FCSTD DOCUMENT  (FreeCAD 0.20R29410 (Git))
Label: wearableV5_April_07_2023
License: All rights reserved
LicenseURL: http://en.wikipedia.org/wiki/All_rights_reserved
objects: Part::Feature×60, Part::Cylinder×20, Part::MultiFuse×15, Sketcher::SketchObject×13, Part::Extrusion×13, Part::Fillet×12, App::Part×9, Part::Box×5, Part::Cut×5, Mesh::Feature×3, Part::Compound×1
note: 144 computed .brp shape members not serialized (recipe doc carries the construction recipe); baked Part::Feature solids carry a one-line shape summary decoded from their .brp

FEATURE [Part::Box] Box  label="battery"
  AttacherType = Attacher::AttachEngine3D
  Height = 11
  Length = 65
  Placement = pos=(4,2,2) rot=(0,0,1;0rad)
  Width = 30
FEATURE [Mesh::Feature] pisugar3Board
  Placement = pos=(-2.89,35.08,0.25) rot=(-1,0,0;4.71239rad)
FEATURE [Part::Feature] Part__Feature001  label="RaspberryPiZeroW"
  Placement = pos=(36.5,17,19.18) rot=(1,0,0;1.5708rad)
  shape: bbox 65.9 x 31.25 x 4.8 mm, 368 faces, 2 solids (baked)
FEATURE [Part::Feature] Part__Feature  label="ips7100"
  Placement = pos=(-24,0,222) rot=(0.999993,-0.003655,0;3.14159rad)
  shape: bbox 48.14 x 14.05 x 44.14 mm, 1935 faces (baked)
FEATURE [Part::Compound] Compound  label="ips7100s"
  Links = -> [Part__Feature]
  Placement = pos=(12.15,32.5,15.79) rot=(0,0.707107,0.707107;3.15032rad)
FEATURE [Part::Feature] Part__Feature002  label="Printed Circuit Board"
  shape: bbox 25.4 x 17.78 x 1.6 mm, 42 faces (baked)
FEATURE [Part::Feature] Part__Feature003  label="EAHC2835WD6"
  shape: bbox 3.513 x 2.813 x 0.7485 mm, 108 faces, 4 solids (baked)
FEATURE [Part::Feature] Part__Feature004  label="AS7341 v2"
  Placement = pos=(0,-0.339822,1.6) rot=(0,0,1;0rad)
  shape: bbox 2 x 3.1 x 1.1 mm, 267 faces, 26 solids (baked)
FEATURE [Part::Feature] Part__Feature005  label="CAPC-0805-T0.95-BN v1"
  Placement = pos=(-5.01759,-3.15294,1.6) rot=(0,0,1;0rad)
  shape: bbox 2.1 x 1.35 x 0.95 mm, 42 faces (baked)
FEATURE [Part::Feature] Part__Feature006  label="CAPC-0805-T0.95-BN v002"
  Placement = pos=(-5.48627,2.66154,1.6) rot=(0,0,-1;1.5708rad)
  shape: bbox 1.35 x 2.1 x 0.95 mm, 42 faces (baked)
FEATURE [Part::Feature] Part__Feature007  label="CAPC-0805-T0.95-BN v003"
  Placement = pos=(-3.43627,2.66154,1.6) rot=(0,0,-1;1.5708rad)
  shape: bbox 1.35 x 2.1 x 0.95 mm, 42 faces (baked)
FEATURE [Part::Feature] Part__Feature008  label="CAPC-0603-T0.9-BN v1"
  Placement = pos=(-1.69987,-3.28475,1.6) rot=(0,0,1;0rad)
  shape: bbox 1.7 x 0.9 x 0.9 mm, 42 faces (baked)
FEATURE [Part::Feature] Part__Feature009  label="BODY_MF06A"
  Placement = pos=(0,0,0.762) rot=(0.57735,-0.57735,-0.57735;2.0944rad)
  shape: bbox 1.601 x 2.921 x 1.016 mm, 42 faces (baked)
FEATURE [Part::Feature] Part__Feature010  label="LEAD_MF06A"
  Placement = pos=(-0.9652,-0.9525,0.1016) rot=(0.57735,-0.57735,-0.57735;2.0944rad)
  shape: bbox 0.6223 x 0.3749 x 0.8636 mm, 14 faces (baked)
FEATURE [Part::Feature] Part__Feature011  label="LEAD_MF06A001"
  Placement = pos=(-0.9652,0,0.1016) rot=(0.57735,-0.57735,-0.57735;2.0944rad)
  shape: bbox 0.6223 x 0.3749 x 0.8636 mm, 14 faces (baked)
FEATURE [Part::Feature] Part__Feature012  label="LEAD_MF06A002"
  Placement = pos=(-0.9652,0.9525,0.1016) rot=(0.57735,-0.57735,-0.57735;2.0944rad)
  shape: bbox 0.6223 x 0.3749 x 0.8636 mm, 14 faces (baked)
FEATURE [Part::Feature] Part__Feature013  label="LEAD_MF06A003"
  Placement = pos=(0.9652,-0.9525,0.1016) rot=(0.57735,0.57735,0.57735;2.0944rad)
  shape: bbox 0.6223 x 0.3749 x 0.8636 mm, 14 faces (baked)
FEATURE [Part::Feature] Part__Feature014  label="LEAD_MF06A004"
  Placement = pos=(0.9652,0,0.1016) rot=(0.57735,0.57735,0.57735;2.0944rad)
  shape: bbox 0.6223 x 0.3749 x 0.8636 mm, 14 faces (baked)
FEATURE [Part::Feature] Part__Feature015  label="LEAD_MF06A005"
  Placement = pos=(0.9652,0.9525,0.1016) rot=(0.57735,0.57735,0.57735;2.0944rad)
  shape: bbox 0.6223 x 0.3749 x 0.8636 mm, 14 faces (baked)
FEATURE [Part::Feature] Part__Feature016  label="SOT363 v2"
  Placement = pos=(4.97054,-0.645171,1.675) rot=(0,0,1;3.14159rad)
  shape: bbox 2.1 x 2 x 1.1 mm, 94 faces, 7 solids (baked)
FEATURE [Part::Feature] Part__Feature017  label="LED 0603 single color v1"
  Placement = pos=(-9.18406,3.72778,1.60762) rot=(0,0,1;1.5708rad)
  shape: bbox 1.961 x 0.7932 x 0.7145 mm, 63 faces, 5 solids (baked)
FEATURE [Part::Feature] Part__Feature018  label="RESC-0603 v1"
  Placement = pos=(4.83432,-3.67461,1.6) rot=(0,0,1;0rad)
  shape: bbox 1.7 x 0.9 x 0.55 mm, 52 faces, 3 solids (baked)
FEATURE [Part::Feature] Part__Feature019  label="RESC-0603 v002"
  Placement = pos=(-7.14949,3.61248,1.6) rot=(0,0,-1;1.5708rad)
  shape: bbox 0.9 x 1.7 x 0.55 mm, 52 faces, 3 solids (baked)
FEATURE [Part::Feature] Part__Feature020  label="YC164_RESPACK v1"
  Placement = pos=(2.99591,1.52916,1.6) rot=(0,0,1;0rad)
  shape: bbox 3.2 x 1.6 x 0.61 mm, 172 faces (baked)
FEATURE [Part::Feature] Part__Feature021  label="qwicc v2"
  Placement = pos=(-10.8364,0.0607456,1.65) rot=(0,0,-1;1.5708rad)
  shape: bbox 4.95 x 6 x 2.96 mm, 229 faces, 7 solids (baked)
FEATURE [Part::Feature] Part__Feature022  label="qwicc v003"
  Placement = pos=(10.8256,0.00556102,1.65) rot=(0,0,1;1.5708rad)
  shape: bbox 4.95 x 6 x 2.96 mm, 229 faces, 7 solids (baked)
FEATURE [Part::Feature] Part__Feature023  label="scd30"
  Placement = pos=(20,54,27) rot=(0.57735,0.57735,-0.57735;4.18879rad)
  shape: bbox 23.02 x 35.11 x 7.027 mm, 2292 faces, 25 solids (baked)
FEATURE [App::Part] sot_23_6_v2  label="sot-23-6 v2"
  Group = -> [Part__Feature009,Part__Feature010,Part__Feature011,Part__Feature012,Part__Feature013,Part__Feature014,Part__Feature015]
  Origin = -> Origin
  Placement = pos=(-4.47945,-0.603742,1.69152) rot=(0,0,1;0rad)
FEATURE [App::Part] Adafruit_AS7341_STEMMA_QT_v2  label="bme280"
  Group = -> [Part__Feature002,Part__Feature003,Part__Feature004,Part__Feature005,Part__Feature006,Part__Feature007,Part__Feature008,sot_23_6_v2,Part__Feature016,Part__Feature017,Part__Feature018,Part__Feature019,Part__Feature020,Part__Feature021,Part__Feature022]
  Origin = -> Origin001
  Placement = pos=(47.7,42,20) rot=(0,0,1;0rad)
FEATURE [Part::Box] Box002  label="bottom"
  AttacherType = Attacher::AttachEngine3D
  Height = 28
  Length = 72
  Width = 81
FEATURE [Part::Fillet] Fillet  label="bottom002"
  Base = -> Box002
  Edges = 8 edges r=2: [Edge1,Edge3,Edge4,Edge5,Edge7,Edge8,Edge9,Edge11]
FEATURE [Part::Box] Box003  label="bottom001"
  AttacherType = Attacher::AttachEngine3D
  Height = 39
  Length = 68
  Placement = pos=(2,2,2) rot=(0,0,1;0rad)
  Width = 77
FEATURE [Part::Fillet] Fillet001  label="bottomCut"
  Base = -> Box003
  Edges = 8 edges r=2: [Edge1,Edge3,Edge4,Edge5,Edge7,Edge8,Edge9,Edge11]
FEATURE [Part::Cut] Cut  label="bottom003"
  Base = -> Fillet
  Tool = -> Fillet001
FEATURE [Part::Cylinder] Cylinder
  Angle = 360
  AttacherType = Attacher::AttachEngine3D
  FirstAngle = 0
  Height = 14
  Placement = pos=(7.25,73.75,2) rot=(0,0,1;0rad)
  Radius = 5
  SecondAngle = 0
FEATURE [Part::Cylinder] Cylinder001
  Angle = 360
  AttacherType = Attacher::AttachEngine3D
  FirstAngle = 0
  Height = 14
  Placement = pos=(64.75,38,2) rot=(0,0,1;0rad)
  Radius = 5
  SecondAngle = 0
FEATURE [Part::Cylinder] Cylinder002
  Angle = 360
  AttacherType = Attacher::AttachEngine3D
  FirstAngle = 0
  Height = 14
  Placement = pos=(7.25,38,2) rot=(0,0,1;0rad)
  Radius = 5
  SecondAngle = 0
FEATURE [Part::Cylinder] Cylinder003
  Angle = 360
  AttacherType = Attacher::AttachEngine3D
  FirstAngle = 0
  Height = 14
  Placement = pos=(64.75,73.75,2) rot=(0,0,1;0rad)
  Radius = 5
  SecondAngle = 0
FEATURE [Part::MultiFuse] Fusion  label="basesBottomIn"
  Shapes = -> [Cylinder003,Cylinder,Cylinder001,Cylinder002]
FEATURE [Part::Feature] Part__Feature024  label="Board"
  shape: bbox 25.4 x 25.4 x 1.57 mm, 211 faces (baked)
FEATURE [Part::Feature] Part__Feature025  label="QFN24_4MM"
  Placement = pos=(12.1412,14.4526,1.57) rot=(0,0,1;3.92699rad)
  shape: bbox 5.657 x 5.657 x 0.9 mm, 172 faces (baked)
FEATURE [Part::Feature] Part__Feature026  label="Part 5"
  shape: bbox 0.48 x 0.6603 x 0.6 mm, 14 faces (baked)
FEATURE [Part::Feature] Part__Feature027  label="Part 6"
  shape: bbox 0.48 x 0.6603 x 0.6 mm, 14 faces (baked)
FEATURE [Part::Feature] Part__Feature028  label="Part 4"
  shape: bbox 0.48 x 0.6603 x 0.6 mm, 14 faces (baked)
FEATURE [Part::Feature] Part__Feature029  label="Part 3"
  shape: bbox 0.48 x 0.6603 x 0.6 mm, 14 faces (baked)
FEATURE [Part::Feature] Part__Feature030  label="Part 2"
  shape: bbox 0.48 x 0.6603 x 0.6 mm, 14 faces (baked)
FEATURE [Part::Feature] Part__Feature031  label="Part 1"
  shape: bbox 3 x 1.4 x 1 mm, 10 faces (baked)
FEATURE [App::Part] _6700497  label="36700497"
  Group = -> [Part__Feature026,Part__Feature027,Part__Feature028,Part__Feature029,Part__Feature030,Part__Feature031]
  Origin = -> Origin002
  Placement = pos=(0,0,0) rot=(0,0,1;3.14159rad)
FEATURE [App::Part] SOT23_5  label="SOT23-5"
  Group = -> [_6700497]
  Origin = -> Origin003
  Placement = pos=(2.54,6.985,1.57) rot=(0,0,1;3.14159rad)
FEATURE [Part::Feature] Part__Feature032  label="Pin1"
  shape: bbox 0.6224 x 1.252 x 1.252 mm, 37 faces (baked)
FEATURE [Part::Feature] Part__Feature033  label="Pin2"
  shape: bbox 0.6224 x 1.252 x 1.252 mm, 37 faces (baked)
FEATURE [Part::Feature] Part__Feature034  label="CeramicBody"
  shape: bbox 1.8 x 1.23 x 1.23 mm, 10 faces (baked)
FEATURE [App::Part] _603_NO  label="0603-NO"
  Group = -> [Part__Feature032,Part__Feature033,Part__Feature034]
  Origin = -> Origin004
  Placement = pos=(16.51,8.382,1.57) rot=(0,0,1;0rad)
FEATURE [Part::Feature] Part__Feature035  label="0603-NO (1)"
  Placement = pos=(23.241,6.223,1.57) rot=(0,0,1;0rad)
  shape: bbox 1.7 x 0.9 x 0.55 mm, 52 faces, 3 solids (baked)
FEATURE [Part::Feature] Part__Feature036  label="0603-NO (2)"
  Placement = pos=(13.3858,8.4328,1.57) rot=(0,0,1;0rad)
  shape: bbox 1.7 x 0.9 x 0.55 mm, 52 faces, 3 solids (baked)
FEATURE [Part::Feature] Part__Feature037  label="0603-NO (3)"
  Placement = pos=(1.905,18.923,1.57) rot=(0,0,1;3.14159rad)
  shape: bbox 1.7 x 0.9 x 0.55 mm, 52 faces, 3 solids (baked)
FEATURE [Part::Feature] Part__Feature038  label="Pin1 (1)"
  shape: bbox 0.6224 x 1.252 x 1.252 mm, 37 faces (baked)
FEATURE [Part::Feature] Part__Feature039  label="Pin2 (1)"
  shape: bbox 0.6224 x 1.252 x 1.252 mm, 37 faces (baked)
FEATURE [Part::Feature] Part__Feature040  label="CeramicBody (1)"
  shape: bbox 1.8 x 1.23 x 1.23 mm, 10 faces (baked)
FEATURE [App::Part] _805_NO  label="0805-NO"
  Group = -> [Part__Feature038,Part__Feature039,Part__Feature040]
  Origin = -> Origin005
  Placement = pos=(7.874,13.589,1.57) rot=(0,0,1;1.5708rad)
FEATURE [Part::Feature] Part__Feature041  label="Pin1 (2)"
  shape: bbox 0.6224 x 1.252 x 1.252 mm, 37 faces (baked)
FEATURE [Part::Feature] Part__Feature042  label="Pin2 (2)"
  shape: bbox 0.6224 x 1.252 x 1.252 mm, 37 faces (baked)
FEATURE [Part::Feature] Part__Feature043  label="CeramicBody (2)"
  shape: bbox 1.8 x 1.23 x 1.23 mm, 10 faces (baked)
FEATURE [App::Part] _805_NO__1_  label="0805-NO (1)"
  Group = -> [Part__Feature041,Part__Feature042,Part__Feature043]
  Origin = -> Origin006
  Placement = pos=(12.827,6.223,1.57) rot=(0,0,1;3.14159rad)
FEATURE [Part::Feature] Part__Feature044  label="CHIPLED_0603_NOOUTLINE"
  Placement = pos=(23.368,8.509,1.57) rot=(0,0,1;1.5708rad)
  shape: bbox 1.616 x 0.8 x 0.4 mm, 133 faces (baked)
FEATURE [Part::Feature] Part__Feature045  label="CHIPLED_0603_NOOUTLINE (1)"
  Placement = pos=(1.905,16.764,1.57) rot=(0,0,-1;1.5708rad)
  shape: bbox 1.616 x 0.8 x 0.4 mm, 133 faces (baked)
FEATURE [Part::Feature] Part__Feature046  label="JST_SH4"
  Placement = pos=(22.86,12.7,1.57) rot=(0,0,1;1.5708rad)
  shape: bbox 4.95 x 6 x 2.96 mm, 229 faces, 7 solids (baked)
FEATURE [Part::Feature] Part__Feature047  label="JST_SH4 (1)"
  Placement = pos=(2.54,12.7,1.57) rot=(0,0,-1;1.5708rad)
  shape: bbox 4.95 x 6 x 2.96 mm, 229 faces, 7 solids (baked)
FEATURE [Part::Feature] Part__Feature048  label="NEO3535_REVERSE"
  Placement = pos=(12.7,23.114,0) rot=(0,1,0;3.14159rad)
  shape: bbox 5.88 x 2.8 x 1.78 mm, 41 faces, 5 solids (baked)
FEATURE [Part::Feature] Part__Feature049  label="RESPACK_4X0603"
  Placement = pos=(22.86,18.415,1.57) rot=(0,0,1;3.14159rad)
  shape: bbox 3.2 x 1.6 x 0.61 mm, 172 faces (baked)
FEATURE [Part::Feature] Part__Feature050  label="SOT363"
  Placement = pos=(17.399,12.192,1.57) rot=(0,0,-1;1.5708rad)
  shape: bbox 2.208 x 2.208 x 1.121 mm, 178 faces, 4 solids (baked)
FEATURE [App::Part] Packages
  Group = -> [Part__Feature025,SOT23_5,_603_NO,Part__Feature035,Part__Feature036,Part__Feature037,_805_NO,_805_NO__1_,Part__Feature044,Part__Feature045,Part__Feature046,Part__Feature047,Part__Feature048,Part__Feature049,Part__Feature050]
  Origin = -> Origin007
FEATURE [App::Part] Adafruit_I2C_QT_Rotary_Encoder_v2  label="gps"
  Group = -> [Part__Feature024,Packages]
  Origin = -> Origin008
  Placement = pos=(35,51,20) rot=(0,0,1;0rad)
FEATURE [Part::Cylinder] Cylinder004
  Angle = 360
  AttacherType = Attacher::AttachEngine3D
  FirstAngle = 0
  Height = 14
  Placement = pos=(7.25,73.75,2) rot=(0,0,1;0rad)
  Radius = 2.1
  SecondAngle = 0
FEATURE [Part::Cylinder] Cylinder005
  Angle = 360
  AttacherType = Attacher::AttachEngine3D
  FirstAngle = 0
  Height = 14
  Placement = pos=(64.75,38,2) rot=(0,0,1;0rad)
  Radius = 2.1
  SecondAngle = 0
FEATURE [Part::Cylinder] Cylinder006
  Angle = 360
  AttacherType = Attacher::AttachEngine3D
  FirstAngle = 0
  Height = 14
  Placement = pos=(7.25,38,2) rot=(0,0,1;0rad)
  Radius = 2.1
  SecondAngle = 0
FEATURE [Part::Cylinder] Cylinder007
  Angle = 360
  AttacherType = Attacher::AttachEngine3D
  FirstAngle = 0
  Height = 14
  Placement = pos=(64.75,73.75,2) rot=(0,0,1;0rad)
  Radius = 2.1
  SecondAngle = 0
FEATURE [Part::MultiFuse] Fusion001  label="basesM4BottomCuts"
  Shapes = -> [Cylinder007,Cylinder004,Cylinder005,Cylinder006]
FEATURE [Sketcher::SketchObject] Sketch
  FullyConstrained = true
  expr: Constraints[40] = 67.75
  sketch-geometry (41):
    g0: LineSegment StartX=2.25 StartY=43 StartZ=0 EndX=2.25 EndY=33 EndZ=0
    g1: LineSegment StartX=2.25 StartY=33 StartZ=0 EndX=67.75 EndY=33 EndZ=0
    g2: LineSegment StartX=2.25 StartY=43 StartZ=0 EndX=8.25 EndY=43 EndZ=0
    g3: LineSegment StartX=2.25 StartY=70 StartZ=0 EndX=8.25 EndY=70 EndZ=0
    g4: LineSegment StartX=2.25 StartY=70 StartZ=0 EndX=2.25 EndY=77 EndZ=0
    g5: ArcOfCircle CenterX=4 CenterY=77 CenterZ=0 NormalX=0 NormalY=0 NormalZ=1 AngleXU=0 Radius=1.75 StartAngle=1.5708 EndAngle=3.14159
    g6: LineSegment StartX=4 StartY=78.75 StartZ=0 EndX=66 EndY=78.75 EndZ=0
    g7: ArcOfCircle CenterX=66 CenterY=77 CenterZ=0 NormalX=0 NormalY=0 NormalZ=1 AngleXU=0 Radius=1.75 StartAngle=1.6e-14 EndAngle=1.5708
    g8: LineSegment StartX=67.75 StartY=77 StartZ=0 EndX=67.75 EndY=70 EndZ=0
    g9: LineSegment StartX=67.75 StartY=70 StartZ=0 EndX=61.75 EndY=70 EndZ=0
    g10: LineSegment StartX=61.75 StartY=70 StartZ=0 EndX=61.75 EndY=43 EndZ=0
    g11: LineSegment StartX=61.75 StartY=43 StartZ=0 EndX=67.75 EndY=43 EndZ=0
    g12: LineSegment StartX=67.75 StartY=43 StartZ=0 EndX=67.75 EndY=33 EndZ=0
    g13: GeomPoint X=67.75 Y=33 Z=0
    g14: GeomPoint X=67.75 Y=33 Z=0
    g15: GeomPoint X=67.75 Y=33 Z=0
    g16: GeomPoint X=67.75 Y=33 Z=0
    g17: GeomPoint X=67.75 Y=33 Z=0
    g18: LineSegment StartX=8.25 StartY=43 StartZ=0 EndX=8.25 EndY=70 EndZ=0
    g19: Circle CenterX=7.25 CenterY=73.75 CenterZ=0 NormalX=0 NormalY=0 NormalZ=1 AngleXU=0 Radius=2.1
    g20: Circle CenterX=7.25 CenterY=38 CenterZ=0 NormalX=0 NormalY=0 NormalZ=1 AngleXU=0 Radius=2.1
    g21: Circle CenterX=64.75 CenterY=38 CenterZ=0 NormalX=0 NormalY=0 NormalZ=1 AngleXU=0 Radius=2.1
    g22: Circle CenterX=64.75 CenterY=73.75 CenterZ=0 NormalX=0 NormalY=0 NormalZ=1 AngleXU=0 Radius=2.1
    g23: Circle CenterX=13.2 CenterY=71.45 CenterZ=0 NormalX=0 NormalY=0 NormalZ=1 AngleXU=0 Radius=1.6
    g24: Circle CenterX=37.54 CenterY=73.86 CenterZ=0 NormalX=0 NormalY=0 NormalZ=1 AngleXU=0 Radius=1.6
    g25: Circle CenterX=57.86 CenterY=73.86 CenterZ=0 NormalX=0 NormalY=0 NormalZ=1 AngleXU=0 Radius=1.6
    g26: Circle CenterX=37.54 CenterY=53.54 CenterZ=0 NormalX=0 NormalY=0 NormalZ=1 AngleXU=0 Radius=1.6
    g27: Circle CenterX=57.86 CenterY=53.54 CenterZ=0 NormalX=0 NormalY=0 NormalZ=1 AngleXU=0 Radius=1.6
    g28: Circle CenterX=37.54 CenterY=48.35 CenterZ=0 NormalX=0 NormalY=0 NormalZ=1 AngleXU=0 Radius=1.6
    g29: Circle CenterX=57.86 CenterY=48.35 CenterZ=0 NormalX=0 NormalY=0 NormalZ=1 AngleXU=0 Radius=1.6
    g30: Circle CenterX=37.54 CenterY=35.65 CenterZ=0 NormalX=0 NormalY=0 NormalZ=1 AngleXU=0 Radius=1.6
    g31: Circle CenterX=57.86 CenterY=35.65 CenterZ=0 NormalX=0 NormalY=0 NormalZ=1 AngleXU=0 Radius=1.6
    g32: Circle CenterX=29.425 CenterY=39.45 CenterZ=0 NormalX=0 NormalY=0 NormalZ=1 AngleXU=0 Radius=1.6
    g33: ArcOfCircle CenterX=46.7 CenterY=66.86 CenterZ=0 NormalX=0 NormalY=0 NormalZ=1 AngleXU=0 Radius=5 StartAngle=2e-16 EndAngle=3.14159
    g34: ArcOfCircle CenterX=46.7 CenterY=42.65 CenterZ=0 NormalX=0 NormalY=0 NormalZ=1 AngleXU=0 Radius=5 StartAngle=3.14159 EndAngle=6.28319
    g35: LineSegment StartX=41.7 StartY=66.86 StartZ=0 EndX=41.7 EndY=42.65 EndZ=0
    g36: LineSegment StartX=51.7 StartY=42.65 StartZ=0 EndX=51.7 EndY=66.86 EndZ=0
    g37: ArcOfCircle CenterX=21.2 CenterY=66.86 CenterZ=0 NormalX=0 NormalY=0 NormalZ=1 AngleXU=0 Radius=5 StartAngle=0 EndAngle=3.14159
    g38: ArcOfCircle CenterX=21.2 CenterY=42.65 CenterZ=0 NormalX=0 NormalY=0 NormalZ=1 AngleXU=0 Radius=5 StartAngle=3.14159 EndAngle=6.28319
    g39: LineSegment StartX=16.2 StartY=66.86 StartZ=0 EndX=16.2 EndY=42.65 EndZ=0
    g40: LineSegment StartX=26.2 StartY=42.65 StartZ=0 EndX=26.2 EndY=66.86 EndZ=0
  constraints (111):
    c: Vertical(g0)
    c: Coincident(g1,g0)
    c: Horizontal(g1)
    c: Coincident(g2,g0)
    c: Coincident(g4,g3)
    c: Vertical(g4)
    c: Coincident(g5,g4)
    c: Horizontal(g6)
    c: Coincident(g7,g6)
    c: Coincident(g8,g7)
    c: Coincident(g9,g8)
    c: Horizontal(g9)
    c: Coincident(g10,g9)
    c: Vertical(g10)
    c: Horizontal(g11)
    c: DistanceX(g-1,g0) = 2.25
    c: Horizontal(g2)
    c: Coincident(g13,g12)
    c: Coincident(g14,g1)
    c: Coincident(g15,g12)
    c: Coincident(g16,g1)
    c: Coincident(g17,g12)
    c: Coincident(g12,g1)
    c: Vertical(g12)
    c: Coincident(g5,g6)
    c: Coincident(g18,g2)
    c: Coincident(g18,g3)
    c: Vertical(g18)
    c: Horizontal(g3)
    c: Vertical(g8)
    c: DistanceY(g0) = 33
    c: DistanceX(g0,g2) = 6
    c: DistanceY(g0,g0) = 10
    c: DistanceX(g3,g3) = 6
    c: DistanceY(g18,g18) = 27
    c: DistanceY(g4,g4) = 7
    c: DistanceY(g5) = 77
    c: Angle(g5) = 1.5708
    c: Radius(g7) = 1.75
    c: Angle(g7) = 1.5708
    c: DistanceX(g1) = 67.75
    c: Coincident(g11,g12)
    c: DistanceY(g1,g11) = 10
    c: Coincident(g10,g11)
    c: DistanceX(g11,g11) = 6
    c: DistanceX(g6,g6) = 62
    c: Radius(g19) = 2.1
    c: DistanceX(g20) = 7.25
    c: DistanceY(g20) = 38
    c: Radius(g20) = 2.1
    c: DistanceX(g21) = 64.75
    c: DistanceY(g20,g21) = 0
    c: Radius(g21) = 2.1
    c: DistanceX(g22,g21) = 0
    c: Radius(g22) = 2.1
    c: DistanceX(g19,g22) = 57.5
    c: DistanceY(g19) = 73.75
    c: DistanceY(g19,g22) = 0
    c: DistanceY(g3,g8) = 0
    c: DistanceX(g5) = 4
    c: DistanceX(g24) = 37.54
    c: Radius(g24) = 1.6
    c: DistanceY(g24,g25) = 0
    c: Radius(g25) = 1.6
    c: DistanceX(g24,g25) = 20.32
    c: DistanceY(g24) = 73.86
    c: DistanceX(g26,g24) = 0
    c: Radius(g26) = 1.6
    c: DistanceY(g26,g24) = 20.32
    c: DistanceY(g27,g26) = 0
    c: DistanceX(g27,g25) = 0
    c: Radius(g27) = 1.6
    c: DistanceX(g28,g26) = 0
    c: DistanceY(g28) = 48.35
    c: Radius(g28) = 1.6
    c: DistanceY(g28,g29) = 0
    c: DistanceX(g27,g29) = 0
    c: Radius(g29) = 1.6
    c: DistanceX(g28,g30) = 0
    c: DistanceX(g31,g29) = 0
    c: DistanceY(g30,g28) = 12.7
    c: DistanceY(g31,g30) = 0
    c: Radius(g31) = 1.6
    c: Radius(g30) = 1.6
    c: Radius(g32) = 1.6
    c: DistanceY(g32) = 39.45
    c: DistanceX(g32) = 29.425
    c: DistanceY(g32,g23) = 32
    c: DistanceX(g23,g32) = 16.225
    c: Radius(g23) = 1.6
    c: Tangent(g33,g35) = -1.5708
    c: Tangent(g35,g34) = -1.5708
    c: Tangent(g34,g36) = -1.5708
    c: Tangent(g36,g33) = -1.5708
    c: Equal(g33,g34)
    c: Vertical(g35)
    c: DistanceX(g33) = 46.7
    c: DistanceY(g33,g24) = 7
    c: DistanceY(g30,g34) = 7
    c: Radius(g33) = 5
    c: Tangent(g37,g39) = -1.5708
    c: Tangent(g39,g38) = -1.5708
    c: Tangent(g38,g40) = -1.5708
    c: Tangent(g40,g37) = -1.5708
    c: Equal(g37,g38)
    c: Vertical(g39)
    c: Radius(g37) = 5
    c: DistanceY(g37,g33) = 0
    c: DistanceY(g34,g38) = 0
    c: DistanceX(g23,g37) = 8
    c: DistanceY(g8,g8) = 7
FEATURE [Part::Extrusion] Extrude  label="sensorHold"
  Base = -> Sketch
  Dir = (0,0,1)
  DirMode = 2
  FaceMakerClass = Part::FaceMakerBullseye
  LengthFwd = 4
  LengthRev = 0
  Placement = pos=(0,0,16) rot=(0,0,1;0rad)
  Solid = true
  Symmetric = false
FEATURE [Part::Fillet] Fillet002  label="sensorHold001"
  Base = -> Extrude
  Edges = 10 edges r=2: [Edge1,Edge2,Edge5,Edge8,Edge11,Edge14,Edge17,Edge20,Edge35,Edge38]
FEATURE [Sketcher::SketchObject] Sketch001
  FullyConstrained = true
  sketch-geometry (10):
    g0: LineSegment StartX=18.03 StartY=72.94 StartZ=0 EndX=18.03 EndY=75.94 EndZ=0
    g1: LineSegment StartX=15.53 StartY=70.44 StartZ=0 EndX=12.53 EndY=70.44 EndZ=0
    g2: LineSegment StartX=12.53 StartY=70.44 StartZ=0 EndX=12.53 EndY=75.94 EndZ=0
    g3: LineSegment StartX=18.03 StartY=75.94 StartZ=0 EndX=12.53 EndY=75.94 EndZ=0
    g4: ArcOfCircle CenterX=15.53 CenterY=72.94 CenterZ=0 NormalX=0 NormalY=0 NormalZ=1 AngleXU=0 Radius=2.5 StartAngle=4.71239 EndAngle=6.28319
    g5: LineSegment StartX=59.53 StartY=33.36 StartZ=0 EndX=54.03 EndY=33.36 EndZ=0
    g6: LineSegment StartX=54.03 StartY=33.36 StartZ=0 EndX=54.03 EndY=36.36 EndZ=0
    g7: LineSegment StartX=59.53 StartY=33.36 StartZ=0 EndX=59.53 EndY=38.86 EndZ=0
    g8: LineSegment StartX=59.53 StartY=38.86 StartZ=0 EndX=56.53 EndY=38.86 EndZ=0
    g9: ArcOfCircle CenterX=56.53 CenterY=36.36 CenterZ=0 NormalX=0 NormalY=0 NormalZ=1 AngleXU=0 Radius=2.5 StartAngle=1.5708 EndAngle=3.14159
  constraints (32):
    c: Vertical(g0)
    c: Horizontal(g1)
    c: Vertical(g2)
    c: Coincident(g2,g3)
    c: Coincident(g0,g3)
    c: Horizontal(g3)
    c: DistanceX(g3,g3) = 5.5
    c: DistanceY(g2,g2) = 5.5
    c: DistanceY(g4,g4) = 0
    c: DistanceX(g4,g4) = 0
    c: Coincident(g1,g4)
    c: Coincident(g0,g4)
    c: Radius(g4) = 2.5
    c: DistanceX(g4) = 15.53
    c: DistanceY(g4) = 72.94
    c: Coincident(g1,g2)
    c: Horizontal(g5)
    c: Vertical(g6)
    c: Vertical(g7)
    c: Horizontal(g8)
    c: Coincident(g7,g8)
    c: Coincident(g8,g9)
    c: Coincident(g6,g9)
    c: Coincident(g5,g6)
    c: Coincident(g5,g7)
    c: DistanceX(g5,g5) = 5.5
    c: DistanceY(g7,g7) = 5.5
    c: DistanceY(g6,g6) = 3
    c: DistanceX(g8,g8) = 3
    c: Radius(g9) = 2.5
    c: DistanceY(g9,g4) = 36.58
    c: DistanceX(g4,g9) = 41
FEATURE [Part::Extrusion] Extrude001
  Base = -> Sketch001
  Dir = (0,0,1)
  DirMode = 2
  FaceMakerClass = Part::FaceMakerBullseye
  LengthFwd = 4
  LengthRev = 0
  Placement = pos=(0,0,2) rot=(0,0,1;0rad)
  Solid = true
  Symmetric = false
FEATURE [Part::Fillet] Fillet003  label="ipsHoldBottomIn"
  Base = -> Extrude001
  Edges = 14 edges r=0.5: [Edge4,Edge7,Edge10,Edge11,Edge13,Edge15,Edge19,Edge20,Edge22,Edge23,Edge25,Edge26,Edge28,Edge30]
FEATURE [Sketcher::SketchObject] Sketch002
  FullyConstrained = true
  MapMode = 2
  Support = -> [Cut]
  sketch-geometry (10):
    g0: LineSegment StartX=62.5 StartY=8.4 StartZ=0 EndX=70.5 EndY=8.4 EndZ=0
    g1: LineSegment StartX=70.5 StartY=8.4 StartZ=0 EndX=70.5 EndY=1.5 EndZ=0
    g2: LineSegment StartX=70.5 StartY=1.5 StartZ=0 EndX=62.5 EndY=1.5 EndZ=0
    g3: LineSegment StartX=62.5 StartY=1.5 StartZ=0 EndX=62.5 EndY=8.4 EndZ=0
    g4: LineSegment StartX=1.5 StartY=9 StartZ=0 EndX=10.75 EndY=9 EndZ=0
    g5: LineSegment StartX=10.75 StartY=9 StartZ=0 EndX=10.75 EndY=1.5 EndZ=0
    g6: LineSegment StartX=10.75 StartY=1.5 StartZ=0 EndX=1.5 EndY=1.5 EndZ=0
    g7: LineSegment StartX=1.5 StartY=1.5 StartZ=0 EndX=1.5 EndY=9 EndZ=0
    g8: Circle CenterX=7.47 CenterY=5.475 CenterZ=0 NormalX=0 NormalY=0 NormalZ=1 AngleXU=0 Radius=1.35
    g9: Circle CenterX=65.52 CenterY=5.475 CenterZ=0 NormalX=0 NormalY=0 NormalZ=1 AngleXU=0 Radius=1.35
  constraints (30):
    c: Coincident(g0,g1)
    c: Coincident(g1,g2)
    c: Coincident(g2,g3)
    c: Coincident(g3,g0)
    c: Horizontal(g0)
    c: Horizontal(g2)
    c: Vertical(g1)
    c: Vertical(g3)
    c: Coincident(g4,g5)
    c: Coincident(g5,g6)
    c: Coincident(g6,g7)
    c: Coincident(g7,g4)
    c: Horizontal(g4)
    c: Horizontal(g6)
    c: Vertical(g5)
    c: Vertical(g7)
    c: DistanceX(g6) = 1.5
    c: DistanceY(g6) = 1.5
    c: DistanceX(g6,g6) = 9.25
    c: DistanceY(g7,g7) = 7.5
    c: DistanceX(g-1,g1) = 70.5
    c: DistanceY(g2,g5) = 0
    c: DistanceY(g0,g4) = 0.6
    c: DistanceX(g2,g2) = 8
    c: DistanceX(g8) = 7.47
    c: Radius(g8) = 1.35
    c: DistanceX(g9) = 65.52
    c: DistanceY(g8,g9) = 0
    c: Radius(g9) = 1.35
    c: DistanceY(g8) = 5.475
FEATURE [Part::Extrusion] Extrude002  label="RaberryPiHold"
  Base = -> Sketch002
  Dir = (0,0,1)
  DirMode = 2
  FaceMakerClass = Part::FaceMakerBullseye
  LengthFwd = 2
  LengthRev = 0
  Placement = pos=(0,0,20.7) rot=(0,0,1;0rad)
  Solid = true
  Symmetric = false
FEATURE [Part::Fillet] Fillet004  label="piHoldBottomIn"
  Base = -> Extrude002
  Edges = 6 edges: [Edge1 r=2,Edge4 r=1,Edge12 r=1,Edge17 r=2,Edge19 r=1,Edge22 r=1]
FEATURE [Part::Box] Box004  label="top"
  AttacherType = Attacher::AttachEngine3D
  Height = 2
  Length = 72
  Placement = pos=(0,0,28) rot=(0,0,1;0rad)
  Width = 81
FEATURE [Part::Fillet] Fillet005  label="top001"
  Base = -> Box004
  Edges = 8 edges r=1.95: [Edge1,Edge2,Edge3,Edge5,Edge6,Edge7,Edge10,Edge12]
FEATURE [Part::Feature] Part__Feature052  label="m4s"
  Placement = pos=(64.75,73.75,14) rot=(1,0,0;3.14159rad)
  shape: bbox 5.501 x 5.501 x 28.29 mm, 108 faces (baked)
FEATURE [Part::Feature] Part__Feature053  label="m4s001"
  Placement = pos=(7.25,73.75,14) rot=(1,0,0;3.14159rad)
  shape: bbox 5.501 x 5.501 x 28.29 mm, 108 faces (baked)
FEATURE [Part::Feature] Part__Feature054  label="m4s002"
  Placement = pos=(64.75,38,14) rot=(1,0,0;3.14159rad)
  shape: bbox 5.501 x 5.501 x 28.29 mm, 108 faces (baked)
FEATURE [Part::Feature] Part__Feature055  label="m4s003"
  Placement = pos=(7.25,38,14) rot=(1,0,0;3.14159rad)
  shape: bbox 5.501 x 5.501 x 28.29 mm, 108 faces (baked)
FEATURE [Part::Cylinder] Cylinder008
  Angle = 360
  AttacherType = Attacher::AttachEngine3D
  FirstAngle = 0
  Height = 7.75
  Placement = pos=(7.25,73.75,2) rot=(0,0,1;0rad)
  Radius = 5
  SecondAngle = 0
FEATURE [Part::Cylinder] Cylinder009
  Angle = 360
  AttacherType = Attacher::AttachEngine3D
  FirstAngle = 0
  Height = 7.75
  Placement = pos=(64.75,38,2) rot=(0,0,1;0rad)
  Radius = 5
  SecondAngle = 0
FEATURE [Part::Cylinder] Cylinder010
  Angle = 360
  AttacherType = Attacher::AttachEngine3D
  FirstAngle = 0
  Height = 7.75
  Placement = pos=(7.25,38,2) rot=(0,0,1;0rad)
  Radius = 5
  SecondAngle = 0
FEATURE [Part::Cylinder] Cylinder011
  Angle = 360
  AttacherType = Attacher::AttachEngine3D
  FirstAngle = 0
  Height = 7.75
  Placement = pos=(64.75,73.75,2) rot=(0,0,1;0rad)
  Radius = 5
  SecondAngle = 0
FEATURE [Part::Feature] Part__Feature056  label="m4Nut"
  Placement = pos=(7.25,38,27) rot=(0,0,1;1.5708rad)
  shape: bbox 8.084 x 8.084 x 2.714 mm, 34 faces (baked)
FEATURE [Part::MultiFuse] Fusion003  label="m4s004"
  Shapes = -> [Part__Feature055,Part__Feature052,Part__Feature053,Part__Feature054]
FEATURE [Part::Feature] Part__Feature057  label="m4Nut001"
  Placement = pos=(64.75,38,27) rot=(0,0,1;1.5708rad)
  shape: bbox 8.084 x 8.084 x 2.714 mm, 34 faces (baked)
FEATURE [Part::MultiFuse] Fusion004
  Shapes = -> [Part__Feature056,Part__Feature057]
FEATURE [Part::Feature] Part__Feature058  label="m4Nut002"
  Placement = pos=(7.25,38,27) rot=(0,0,1;1.5708rad)
  shape: bbox 8.084 x 8.084 x 2.714 mm, 34 faces (baked)
FEATURE [Part::Feature] Part__Feature059  label="m4Nut003"
  Placement = pos=(64.75,38,27) rot=(0,0,1;1.5708rad)
  shape: bbox 8.084 x 8.084 x 2.714 mm, 34 faces (baked)
FEATURE [Part::MultiFuse] Fusion005
  Placement = pos=(0,35.75,0) rot=(0,0,1;0rad)
  Shapes = -> [Part__Feature058,Part__Feature059]
FEATURE [Part::MultiFuse] Fusion006  label="m4Nuts"
  Placement = pos=(0,0,-1) rot=(0,0,1;0rad)
  Shapes = -> [Fusion005,Fusion004]
FEATURE [Sketcher::SketchObject] Sketch003
  FullyConstrained = true
  MapMode = 2
  Placement = pos=(70,0,30) rot=(0,1,0;3.14159rad)
  sketch-geometry (36):
    g0: LineSegment StartX=3.125 StartY=34.3194 StartZ=0 EndX=7.375 EndY=34.3194 EndZ=0
    g1: LineSegment StartX=7.375 StartY=34.3194 StartZ=0 EndX=7.47604 EndY=34.4944 EndZ=0
    g2: LineSegment StartX=3.125 StartY=34.3194 StartZ=0 EndX=1 EndY=38 EndZ=0
    g3: LineSegment StartX=1 StartY=38 StartZ=0 EndX=3.125 EndY=41.6806 EndZ=0
    g4: LineSegment StartX=3.125 StartY=41.6806 StartZ=0 EndX=7.375 EndY=41.6806 EndZ=0
    g5: LineSegment StartX=7.375 StartY=41.6806 StartZ=0 EndX=7.47604 EndY=41.5056 EndZ=0
    g6: LineSegment StartX=7.47604 StartY=41.5056 StartZ=0 EndX=10.476 EndY=41.5056 EndZ=0
    g7: LineSegment StartX=10.476 StartY=41.5056 StartZ=0 EndX=10.476 EndY=34.4944 EndZ=0
    g8: LineSegment StartX=10.476 StartY=34.4944 StartZ=0 EndX=7.47604 EndY=34.4944 EndZ=0
    g9: LineSegment StartX=60.524 StartY=34.4944 StartZ=0 EndX=60.625 EndY=34.3194 EndZ=0
    g10: LineSegment StartX=60.625 StartY=34.3194 StartZ=0 EndX=64.875 EndY=34.3194 EndZ=0
    g11: LineSegment StartX=64.875 StartY=34.3194 StartZ=0 EndX=67 EndY=38 EndZ=0
    g12: LineSegment StartX=67 StartY=38 StartZ=0 EndX=64.875 EndY=41.6806 EndZ=0
    g13: LineSegment StartX=64.875 StartY=41.6806 StartZ=0 EndX=60.625 EndY=41.6806 EndZ=0
    g14: LineSegment StartX=60.625 StartY=41.6806 StartZ=0 EndX=60.524 EndY=41.5056 EndZ=0
    g15: LineSegment StartX=60.524 StartY=41.5056 StartZ=0 EndX=57.524 EndY=41.5056 EndZ=0
    g16: LineSegment StartX=57.524 StartY=41.5056 StartZ=0 EndX=57.524 EndY=34.4944 EndZ=0
    g17: LineSegment StartX=57.524 StartY=34.4944 StartZ=0 EndX=60.524 EndY=34.4944 EndZ=0
    g18: LineSegment StartX=1 StartY=73.75 StartZ=0 EndX=3.125 EndY=70.0694 EndZ=0
    g19: LineSegment StartX=3.125 StartY=70.0694 StartZ=0 EndX=7.375 EndY=70.0694 EndZ=0
    g20: LineSegment StartX=7.375 StartY=70.0694 StartZ=0 EndX=7.47604 EndY=70.2444 EndZ=0
    g21: LineSegment StartX=7.47604 StartY=70.2444 StartZ=0 EndX=10.476 EndY=70.2444 EndZ=0
    g22: LineSegment StartX=10.476 StartY=70.2444 StartZ=0 EndX=10.476 EndY=77.2556 EndZ=0
    g23: LineSegment StartX=10.476 StartY=77.2556 StartZ=0 EndX=7.47604 EndY=77.2556 EndZ=0
    g24: LineSegment StartX=7.47604 StartY=77.2556 StartZ=0 EndX=7.375 EndY=77.4306 EndZ=0
    g25: LineSegment StartX=7.375 StartY=77.4306 StartZ=0 EndX=3.125 EndY=77.4306 EndZ=0
    g26: LineSegment StartX=3.125 StartY=77.4306 StartZ=0 EndX=1 EndY=73.75 EndZ=0
    g27: LineSegment StartX=67 StartY=73.75 StartZ=0 EndX=64.875 EndY=70.0694 EndZ=0
    g28: LineSegment StartX=64.875 StartY=70.0694 StartZ=0 EndX=60.625 EndY=70.0694 EndZ=0
    g29: LineSegment StartX=60.625 StartY=70.0694 StartZ=0 EndX=60.524 EndY=70.2444 EndZ=0
    g30: LineSegment StartX=60.524 StartY=70.2444 StartZ=0 EndX=57.524 EndY=70.2444 EndZ=0
    g31: LineSegment StartX=57.524 StartY=70.2444 StartZ=0 EndX=57.524 EndY=77.2556 EndZ=0
    g32: LineSegment StartX=57.524 StartY=77.2556 StartZ=0 EndX=60.524 EndY=77.2556 EndZ=0
    g33: LineSegment StartX=60.524 StartY=77.2556 StartZ=0 EndX=60.625 EndY=77.4306 EndZ=0
    g34: LineSegment StartX=60.625 StartY=77.4306 StartZ=0 EndX=64.875 EndY=77.4306 EndZ=0
    g35: LineSegment StartX=64.875 StartY=77.4306 StartZ=0 EndX=67 EndY=73.75 EndZ=0
  constraints (108):
    c: Horizontal(g0)
    c: Coincident(g1,g0)
    c: Coincident(g2,g0)
    c: Coincident(g4,g3)
    c: Horizontal(g4)
    c: Coincident(g5,g4)
    c: Coincident(g6,g5)
    c: Horizontal(g6)
    c: Coincident(g7,g6)
    c: Vertical(g7)
    c: Coincident(g8,g7)
    c: Coincident(g8,g1)
    c: Angle(g0,g2) = 2.0944
    c: Coincident(g2,g3)
    c: Distance(g2) = 4.25
    c: Distance(g3) = 4.25
    c: DistanceY(g2) = 38
    c: Angle(g3,g4) = 2.0944
    c: DistanceX(g2) = 1
    c: Distance(g4) = 4.25
    c: Distance(g0) = 4.25
    c: Angle(g4,g5) = 2.0944
    c: Angle(g1,g0) = 2.0944
    c: DistanceY(g1,g1) = 0.175
    c: Horizontal(g8)
    c: DistanceX(g8,g8) = 3
    c: Coincident(g10,g9)
    c: Horizontal(g10)
    c: Coincident(g11,g10)
    c: Coincident(g15,g14)
    c: Horizontal(g15)
    c: Coincident(g16,g15)
    c: Vertical(g16)
    c: Coincident(g17,g16)
    c: Coincident(g17,g9)
    c: Horizontal(g17)
    c: Angle(g11,g10) = 2.0944
    c: Angle(g12,g11) = 2.0944
    c: Coincident(g11,g12)
    c: Angle(g13,g12) = 2.0944
    c: Coincident(g13,g14)
    c: Coincident(g12,g13)
    c: Angle(g14,g13) = 2.0944
    c: Angle(g10,g9) = 2.0944
    c: DistanceX(g14,g9) = 0
    c: DistanceX(g13,g9) = 0
    c: Distance(g10) = 4.25
    c: Distance(g11) = 4.25
    c: Distance(g13) = 4.25
    c: DistanceX(g17,g17) = 3
    c: DistanceY(g5,g4) = 0.175
    c: DistanceX(g2,g11) = 66
    c: DistanceY(g11,g2) = 0
    c: DistanceY(g15,g6) = 0
    c: Coincident(g18,g19)
    c: Horizontal(g19)
    c: Coincident(g19,g20)
    c: Coincident(g20,g21)
    c: Horizontal(g21)
    c: Coincident(g21,g22)
    c: Vertical(g22)
    c: Coincident(g22,g23)
    c: Coincident(g23,g24)
    c: Coincident(g24,g25)
    c: Horizontal(g25)
    c: Coincident(g25,g26)
    c: Coincident(g26,g18)
    c: DistanceX(g18,g2) = 0
    c: DistanceY(g2,g18) = 35.75
    c: Angle(g18,g26) = 2.0944
    c: Angle(g26,g25) = 2.0944
    c: Angle(g20,g19) = 2.0944
    c: Angle(g25,g24) = 2.0944
    c: DistanceY(g23,g24) = 0.175
    c: DistanceY(g19,g20) = 0.175
    c: Distance(g21) = 3
    c: Horizontal(g23)
    c: Coincident(g27,g28)
    c: Horizontal(g28)
    c: Coincident(g28,g29)
    c: Coincident(g29,g30)
    c: Horizontal(g30)
    c: Coincident(g30,g31)
    c: Vertical(g31)
    c: Coincident(g31,g32)
    c: Horizontal(g32)
    c: Coincident(g32,g33)
    c: Coincident(g33,g34)
    c: Horizontal(g34)
    c: Coincident(g34,g35)
    c: Coincident(g35,g27)
    c: DistanceX(g11,g27) = 0
    c: DistanceY(g18,g27) = 0
    c: Angle(g27,g28) = 2.0944
    c: Angle(g35,g27) = 2.0944
    c: Angle(g33,g34) = 2.0944
    c: DistanceX(g32,g32) = 3
    c: Angle(g28,g29) = 2.0944
    c: DistanceY(g28,g29) = 0.175
    c: DistanceY(g32,g33) = 0.175
    c: DistanceX(g30,g15) = 0
    c: Distance(g18) = 4.25
    c: Distance(g26) = 4.25
    c: Distance(g19) = 4.25
    c: Distance(g25) = 4.25
    c: Distance(g28) = 4.25
    c: Distance(g27) = 4.25
    c: Distance(g35) = 4.25
FEATURE [Part::Extrusion] Extrude003  label="m4InletTopCut"
  Base = -> Sketch003
  Dir = (0,0,-1)
  DirMode = 2
  FaceMakerClass = Part::FaceMakerBullseye
  LengthFwd = 2.5
  LengthRev = 0
  Placement = pos=(0,0,-2.75) rot=(0,0,1;0rad)
  Solid = true
  Symmetric = false
FEATURE [Part::Box] Box005  label="baseTopCut"
  AttacherType = Attacher::AttachEngine3D
  Height = 8
  Length = 51
  Placement = pos=(10.5,33.5,20) rot=(0,0,1;0rad)
  Width = 44
FEATURE [Part::Feature] Part__Feature060  label="logoTopCut"
  Placement = pos=(25,-2,35) rot=(-1,0,0;1.5708rad)
  shape: bbox 22.79 x 17.08 x 8 mm, 886 faces (baked)
FEATURE [Mesh::Feature] mintsLogo80P___90CutBase  label="mintsLogo80P - 90CutBase"
  Placement = pos=(56.35,12.9,26) rot=(0,0,1;0rad)
FEATURE [Part::Cylinder] Cylinder012
  Angle = 360
  AttacherType = Attacher::AttachEngine3D
  FirstAngle = 0
  Height = 3.15
  Placement = pos=(7.25,73.75,2) rot=(0,0,1;0rad)
  Radius = 3.6
  SecondAngle = 0
FEATURE [Part::Cylinder] Cylinder013
  Angle = 360
  AttacherType = Attacher::AttachEngine3D
  FirstAngle = 0
  Height = 3.15
  Placement = pos=(64.75,38,2) rot=(0,0,1;0rad)
  Radius = 3.6
  SecondAngle = 0
FEATURE [Part::Cylinder] Cylinder014
  Angle = 360
  AttacherType = Attacher::AttachEngine3D
  FirstAngle = 0
  Height = 3.15
  Placement = pos=(7.25,38,2) rot=(0,0,1;0rad)
  Radius = 3.6
  SecondAngle = 0
FEATURE [Part::Cylinder] Cylinder015
  Angle = 360
  AttacherType = Attacher::AttachEngine3D
  FirstAngle = 0
  Height = 3.15
  Placement = pos=(64.75,73.75,2) rot=(0,0,1;0rad)
  Radius = 3.6
  SecondAngle = 0
FEATURE [Part::MultiFuse] Fusion007  label="m4headBottomCut"
  Placement = pos=(0,0,-2) rot=(0,0,1;0rad)
  Shapes = -> [Cylinder015,Cylinder012,Cylinder013,Cylinder014]
FEATURE [Sketcher::SketchObject] Sketch004
  FullyConstrained = true
  Placement = pos=(0,0,0) rot=(1,0,0;1.5708rad)
  sketch-geometry (34):
    g0: ArcOfCircle CenterX=13.55 CenterY=15.58 CenterZ=0 NormalX=0 NormalY=0 NormalZ=1 AngleXU=0 Radius=2 StartAngle=1.5708 EndAngle=4.71239
    g1: ArcOfCircle CenterX=15.55 CenterY=15.58 CenterZ=0 NormalX=0 NormalY=0 NormalZ=1 AngleXU=0 Radius=2 StartAngle=4.71239 EndAngle=7.85398
    g2: LineSegment StartX=13.55 StartY=13.58 StartZ=0 EndX=15.55 EndY=13.58 EndZ=0
    g3: LineSegment StartX=15.55 StartY=17.58 StartZ=0 EndX=13.55 EndY=17.58 EndZ=0
    g4: ArcOfCircle CenterX=46.02 CenterY=15.58 CenterZ=0 NormalX=0 NormalY=0 NormalZ=1 AngleXU=0 Radius=2 StartAngle=1.5708 EndAngle=4.71239
    g5: ArcOfCircle CenterX=48.02 CenterY=15.58 CenterZ=0 NormalX=0 NormalY=0 NormalZ=1 AngleXU=0 Radius=2 StartAngle=4.71239 EndAngle=7.85398
    g6: LineSegment StartX=46.02 StartY=13.58 StartZ=0 EndX=48.02 EndY=13.58 EndZ=0
    g7: LineSegment StartX=48.02 StartY=17.58 StartZ=0 EndX=46.02 EndY=17.58 EndZ=0
    g8: ArcOfCircle CenterX=18.75 CenterY=16.35 CenterZ=0 NormalX=0 NormalY=0 NormalZ=1 AngleXU=0 Radius=0.5 StartAngle=1.5708 EndAngle=4.71239
    g9: ArcOfCircle CenterX=25.7 CenterY=16.35 CenterZ=0 NormalX=0 NormalY=0 NormalZ=1 AngleXU=0 Radius=0.5 StartAngle=4.71239 EndAngle=7.85398
    g10: LineSegment StartX=18.75 StartY=15.85 StartZ=0 EndX=25.7 EndY=15.85 EndZ=0
    g11: LineSegment StartX=25.7 StartY=16.85 StartZ=0 EndX=18.75 EndY=16.85 EndZ=0
    g12: ArcOfCircle CenterX=53.5 CenterY=15.1 CenterZ=0 NormalX=0 NormalY=0 NormalZ=1 AngleXU=0 Radius=2.5 StartAngle=1.5708 EndAngle=4.71239
    g13: ArcOfCircle CenterX=60.5 CenterY=15.1 CenterZ=0 NormalX=0 NormalY=0 NormalZ=1 AngleXU=0 Radius=2.5 StartAngle=4.71239 EndAngle=7.85398
    g14: LineSegment StartX=53.5 StartY=12.6 StartZ=0 EndX=60.5 EndY=12.6 EndZ=0
    g15: LineSegment StartX=60.5 StartY=17.6 StartZ=0 EndX=53.5 EndY=17.6 EndZ=0
    g16: LineSegment StartX=11.75 StartY=19.5 StartZ=0 EndX=21.5 EndY=19.5 EndZ=0
    g17: LineSegment StartX=21.5 StartY=19.5 StartZ=0 EndX=23.75 EndY=22 EndZ=0
    g18: LineSegment StartX=23.75 StartY=22 StartZ=0 EndX=23.75 EndY=25 EndZ=0
    g19: LineSegment StartX=23.75 StartY=25 StartZ=0 EndX=9.5 EndY=25 EndZ=0
    g20: LineSegment StartX=9.5 StartY=25 StartZ=0 EndX=9.5 EndY=22 EndZ=0
    g21: LineSegment StartX=40 StartY=24.5 StartZ=0 EndX=40 EndY=22 EndZ=0
    g22: LineSegment StartX=40 StartY=22 StartZ=0 EndX=42.5 EndY=19.5 EndZ=0
    g23: LineSegment StartX=42.5 StartY=19.5 StartZ=0 EndX=48.7 EndY=19.5 EndZ=0
    g24: LineSegment StartX=48.7 StartY=19.5 StartZ=0 EndX=51.2 EndY=22 EndZ=0
    g25: LineSegment StartX=51.2 StartY=22 StartZ=0 EndX=51.2 EndY=24.5 EndZ=0
    g26: LineSegment StartX=51.2 StartY=24.5 StartZ=0 EndX=40 EndY=24.5 EndZ=0
    g27: LineSegment StartX=52.45 StartY=24.5 StartZ=0 EndX=52.45 EndY=22 EndZ=0
    g28: LineSegment StartX=52.45 StartY=22 StartZ=0 EndX=54.95 EndY=19.5 EndZ=0
    g29: LineSegment StartX=54.95 StartY=19.5 StartZ=0 EndX=61.15 EndY=19.5 EndZ=0
    g30: LineSegment StartX=61.15 StartY=19.5 StartZ=0 EndX=63.65 EndY=22 EndZ=0
    g31: LineSegment StartX=63.65 StartY=22 StartZ=0 EndX=63.65 EndY=24.5 EndZ=0
    g32: LineSegment StartX=63.65 StartY=24.5 StartZ=0 EndX=52.45 EndY=24.5 EndZ=0
    g33: LineSegment StartX=9.5 StartY=22 StartZ=0 EndX=11.75 EndY=19.5 EndZ=0
  constraints (94):
    c: Tangent(g0,g2) = -1.5708
    c: Tangent(g2,g1) = -1.5708
    c: Tangent(g1,g3) = -1.5708
    c: Tangent(g3,g0) = -1.5708
    c: Equal(g0,g1)
    c: Horizontal(g2)
    c: DistanceX(g0) = 13.55
    c: DistanceX(g0,g1) = 2
    c: DistanceY(g0) = 15.58
    c: DistanceY(g0,g0) = 4
    c: Tangent(g4,g6) = -1.5708
    c: Tangent(g6,g5) = -1.5708
    c: Tangent(g5,g7) = -1.5708
    c: Tangent(g7,g4) = -1.5708
    c: Equal(g4,g5)
    c: Horizontal(g6)
    c: DistanceY(g4,g1) = 0
    c: DistanceX(g4,g5) = 2
    c: DistanceX(g1,g4) = 30.47
    c: DistanceY(g4,g4) = 4
    c: Tangent(g8,g10) = -1.5708
    c: Tangent(g10,g9) = -1.5708
    c: Tangent(g9,g11) = -1.5708
    c: Tangent(g11,g8) = -1.5708
    c: Equal(g8,g9)
    c: Horizontal(g10)
    c: DistanceX(g8) = 18.75
    c: DistanceY(g8,g8) = 1
    c: DistanceX(g8,g9) = 6.95
    c: DistanceY(g8) = 16.35
    c: Tangent(g12,g14) = -1.5708
    c: Tangent(g14,g13) = -1.5708
    c: Tangent(g13,g15) = -1.5708
    c: Tangent(g15,g12) = -1.5708
    c: Equal(g12,g13)
    c: Horizontal(g14)
    c: DistanceX(g12) = 53.5
    c: DistanceX(g12,g13) = 7
    c: DistanceY(g12) = 15.1
    c: DistanceY(g12,g12) = 5
    c: Horizontal(g16)
    c: Coincident(g16,g17)
    c: Coincident(g17,g18)
    c: Coincident(g18,g19)
    c: Horizontal(g19)
    c: Coincident(g19,g20)
    c: Vertical(g20)
    c: Coincident(g21,g22)
    c: Coincident(g22,g23)
    c: Horizontal(g23)
    c: Coincident(g23,g24)
    c: Coincident(g24,g25)
    c: Vertical(g25)
    c: Coincident(g25,g26)
    c: Coincident(g26,g21)
    c: Coincident(g27,g28)
    c: Coincident(g28,g29)
    c: Horizontal(g29)
    c: Coincident(g29,g30)
    c: Coincident(g30,g31)
    c: Vertical(g31)
    c: Coincident(g31,g32)
    c: Coincident(g32,g27)
    c: Horizontal(g32)
    c: Coincident(g33,g20)
    c: Coincident(g16,g33)
    c: DistanceX(g19) = 9.5
    c: DistanceX(g19,g19) = 14.25
    c: Vertical(g18)
    c: DistanceY(g19) = 25
    c: DistanceY(g20) = 22
    c: DistanceY(g20,g17) = 0
    c: DistanceX(g20,g16) = 2.25
    c: DistanceX(g16,g17) = 2.25
    c: Horizontal(g26)
    c: Vertical(g21)
    c: Vertical(g27)
    c: DistanceX(g21) = 40
    c: DistanceX(g21,g25) = 11.2
    c: DistanceY(g27,g25) = 0
    c: DistanceY(g21,g21) = 2.5
    c: DistanceY(g24,g21) = 0
    c: DistanceY(g27,g24) = 0
    c: DistanceY(g30,g27) = 0
    c: DistanceY(g22,g21) = 2.5
    c: DistanceX(g21,g22) = 2.5
    c: DistanceX(g23,g24) = 2.5
    c: DistanceX(g25,g27) = 1.25
    c: DistanceY(g28,g23) = 0
    c: DistanceX(g27,g28) = 2.5
    c: DistanceX(g29,g30) = 2.5
    c: DistanceX(g27,g31) = 11.2
    c: DistanceY(g16,g20) = 2.5
    c: DistanceY(g21) = 24.5
FEATURE [Part::Extrusion] Extrude004  label="lightBottomCut"
  Base = -> Sketch004
  Dir = (0,-1,2e-16)
  DirMode = 2
  FaceMakerClass = Part::FaceMakerBullseye
  LengthFwd = 2
  LengthRev = 0
  Placement = pos=(0,2,0) rot=(0,0,1;0rad)
  Solid = true
  Symmetric = false
FEATURE [Sketcher::SketchObject] Sketch005
  FullyConstrained = true
  Placement = pos=(0,0,0) rot=(1,0,0;1.5708rad)
  sketch-geometry (4):
    g0: ArcOfCircle CenterX=16.9 CenterY=16.35 CenterZ=0 NormalX=0 NormalY=0 NormalZ=1 AngleXU=0 Radius=1 StartAngle=1.5708 EndAngle=4.71239
    g1: ArcOfCircle CenterX=23.5 CenterY=16.35 CenterZ=0 NormalX=0 NormalY=0 NormalZ=1 AngleXU=0 Radius=1 StartAngle=4.71239 EndAngle=7.85398
    g2: LineSegment StartX=16.9 StartY=15.35 StartZ=0 EndX=23.5 EndY=15.35 EndZ=0
    g3: LineSegment StartX=23.5 StartY=17.35 StartZ=0 EndX=16.9 EndY=17.35 EndZ=0
  constraints (10):
    c: Tangent(g0,g2) = -1.5708
    c: Tangent(g2,g1) = -1.5708
    c: Tangent(g1,g3) = -1.5708
    c: Tangent(g3,g0) = -1.5708
    c: Equal(g0,g1)
    c: Horizontal(g2)
    c: DistanceX(g0) = 16.9
    c: DistanceY(g0,g0) = 2
    c: DistanceX(g0,g1) = 6.6
    c: DistanceY(g0) = 16.35
FEATURE [Sketcher::SketchObject] Sketch006
  FullyConstrained = true
  Placement = pos=(0,0,0) rot=(1,0,0;1.5708rad)
  sketch-geometry (4):
    g0: ArcOfCircle CenterX=16.9 CenterY=14.75 CenterZ=0 NormalX=0 NormalY=0 NormalZ=1 AngleXU=0 Radius=1 StartAngle=1.5708 EndAngle=4.71239
    g1: ArcOfCircle CenterX=23.5 CenterY=14.75 CenterZ=0 NormalX=0 NormalY=0 NormalZ=1 AngleXU=0 Radius=1 StartAngle=4.71239 EndAngle=7.85398
    g2: LineSegment StartX=16.9 StartY=13.75 StartZ=0 EndX=23.5 EndY=13.75 EndZ=0
    g3: LineSegment StartX=23.5 StartY=15.75 StartZ=0 EndX=16.9 EndY=15.75 EndZ=0
  constraints (10):
    c: Tangent(g0,g2) = -1.5708
    c: Tangent(g2,g1) = -1.5708
    c: Tangent(g1,g3) = -1.5708
    c: Tangent(g3,g0) = -1.5708
    c: Equal(g0,g1)
    c: Horizontal(g2)
    c: DistanceX(g0) = 16.9
    c: DistanceY(g0,g0) = 2
    c: DistanceX(g0,g1) = 6.6
    c: DistanceY(g0) = 14.75
FEATURE [Part::Extrusion] Extrude005
  Base = -> Sketch005
  Dir = (0,-1,2e-16)
  DirMode = 2
  FaceMakerClass = Part::FaceMakerBullseye
  LengthFwd = 2.25
  LengthRev = 0
  Placement = pos=(0,2,0) rot=(0,0,1;0rad)
  Solid = true
  Symmetric = false
FEATURE [Part::Extrusion] Extrude006
  Base = -> Sketch006
  Dir = (0,-1,2e-16)
  DirMode = 2
  FaceMakerClass = Part::FaceMakerBullseye
  LengthFwd = 2
  LengthRev = 0
  Placement = pos=(0,4,0) rot=(0,0,1;0rad)
  Solid = true
  Symmetric = false
FEATURE [Part::MultiFuse] Fusion008  label="lightInlet"
  Placement = pos=(0,0.25,0) rot=(0,0,1;0rad)
  Shapes = -> [Extrude005,Extrude006]
FEATURE [Sketcher::SketchObject] Sketch007
  FullyConstrained = true
  sketch-geometry (48):
    g0: LineSegment StartX=4 StartY=77 StartZ=0 EndX=6 EndY=77 EndZ=0
    g1: LineSegment StartX=6 StartY=77 StartZ=0 EndX=-3.99999 EndY=59.6795 EndZ=0
    g2: LineSegment StartX=-3.99999 StartY=59.6795 StartZ=0 EndX=-5.99999 EndY=59.6795 EndZ=0
    g3: LineSegment StartX=-5.99999 StartY=59.6795 StartZ=0 EndX=4 EndY=77 EndZ=0
    g4: LineSegment StartX=-5.99999 StartY=52.6795 StartZ=0 EndX=-3.99999 EndY=52.6795 EndZ=0
    g5: LineSegment StartX=-5.99999 StartY=52.6795 StartZ=0 EndX=4 EndY=70 EndZ=0
    g6: LineSegment StartX=4 StartY=70 StartZ=0 EndX=6 EndY=70 EndZ=0
    g7: LineSegment StartX=6 StartY=70 StartZ=0 EndX=-3.99999 EndY=52.6795 EndZ=0
    g8: LineSegment StartX=-3.99999 StartY=45.6795 StartZ=0 EndX=-5.99999 EndY=45.6795 EndZ=0
    g9: LineSegment StartX=-5.99999 StartY=45.6795 StartZ=0 EndX=4 EndY=63 EndZ=0
    g10: LineSegment StartX=4 StartY=63 StartZ=0 EndX=6 EndY=63 EndZ=0
    g11: LineSegment StartX=6 StartY=63 StartZ=0 EndX=-3.99999 EndY=45.6795 EndZ=0
    g12: LineSegment StartX=4 StartY=56 StartZ=0 EndX=6 EndY=56 EndZ=0
    g13: LineSegment StartX=6 StartY=56 StartZ=0 EndX=-3.99999 EndY=38.6795 EndZ=0
    g14: LineSegment StartX=-3.99999 StartY=38.6795 StartZ=0 EndX=-5.99999 EndY=38.6795 EndZ=0
    g15: LineSegment StartX=-5.99999 StartY=38.6795 StartZ=0 EndX=4 EndY=56 EndZ=0
    g16: LineSegment StartX=4 StartY=49 StartZ=0 EndX=6 EndY=49 EndZ=0
    g17: LineSegment StartX=6 StartY=49 StartZ=0 EndX=-3.99999 EndY=31.6795 EndZ=0
    g18: LineSegment StartX=-3.99999 StartY=31.6795 StartZ=0 EndX=-5.99999 EndY=31.6795 EndZ=0
    g19: LineSegment StartX=-5.99999 StartY=31.6795 StartZ=0 EndX=4 EndY=49 EndZ=0
    g20: LineSegment StartX=4 StartY=42 StartZ=0 EndX=6 EndY=42 EndZ=0
    g21: LineSegment StartX=6 StartY=42 StartZ=0 EndX=-3.99999 EndY=24.6795 EndZ=0
    g22: LineSegment StartX=-3.99999 StartY=24.6795 StartZ=0 EndX=-5.99999 EndY=24.6795 EndZ=0
    g23: LineSegment StartX=-5.99999 StartY=24.6795 StartZ=0 EndX=4 EndY=42 EndZ=0
    g24: LineSegment StartX=68 StartY=77 StartZ=0 EndX=66 EndY=77 EndZ=0
    g25: LineSegment StartX=66 StartY=77 StartZ=0 EndX=76 EndY=59.6795 EndZ=0
    g26: LineSegment StartX=76 StartY=59.6795 StartZ=0 EndX=78 EndY=59.6795 EndZ=0
    g27: LineSegment StartX=78 StartY=59.6795 StartZ=0 EndX=68 EndY=77 EndZ=0
    g28: LineSegment StartX=66 StartY=70 StartZ=0 EndX=68 EndY=70 EndZ=0
    g29: LineSegment StartX=68 StartY=70 StartZ=0 EndX=78 EndY=52.6795 EndZ=0
    g30: LineSegment StartX=78 StartY=52.6795 StartZ=0 EndX=76 EndY=52.6795 EndZ=0
    g31: LineSegment StartX=76 StartY=52.6795 StartZ=0 EndX=66 EndY=70 EndZ=0
    g32: LineSegment StartX=66 StartY=63 StartZ=0 EndX=68 EndY=63 EndZ=0
    g33: LineSegment StartX=68 StartY=63 StartZ=0 EndX=78 EndY=45.6795 EndZ=0
    g34: LineSegment StartX=78 StartY=45.6795 StartZ=0 EndX=76 EndY=45.6795 EndZ=0
    g35: LineSegment StartX=76 StartY=45.6795 StartZ=0 EndX=66 EndY=63 EndZ=0
    g36: LineSegment StartX=66 StartY=56 StartZ=0 EndX=68 EndY=56 EndZ=0
    g37: LineSegment StartX=68 StartY=56 StartZ=0 EndX=78 EndY=38.6795 EndZ=0
    g38: LineSegment StartX=78 StartY=38.6795 StartZ=0 EndX=76 EndY=38.6795 EndZ=0
    g39: LineSegment StartX=76 StartY=38.6795 StartZ=0 EndX=66 EndY=56 EndZ=0
    g40: LineSegment StartX=66 StartY=49 StartZ=0 EndX=68 EndY=49 EndZ=0
    g41: LineSegment StartX=68 StartY=49 StartZ=0 EndX=78 EndY=31.6795 EndZ=0
    g42: LineSegment StartX=78 StartY=31.6795 StartZ=0 EndX=76 EndY=31.6795 EndZ=0
    g43: LineSegment StartX=76 StartY=31.6795 StartZ=0 EndX=66 EndY=49 EndZ=0
    g44: LineSegment StartX=66 StartY=42 StartZ=0 EndX=68 EndY=42 EndZ=0
    g45: LineSegment StartX=68 StartY=42 StartZ=0 EndX=78 EndY=24.6795 EndZ=0
    g46: LineSegment StartX=78 StartY=24.6795 StartZ=0 EndX=76 EndY=24.6795 EndZ=0
    g47: LineSegment StartX=76 StartY=24.6795 StartZ=0 EndX=66 EndY=42 EndZ=0
  constraints (144):
    c: Coincident(g3,g0)
    c: DistanceX(g2,g2) = 2
    c: DistanceX(g0,g0) = 2
    c: Angle(g1) = -2.0944
    c: Distance(g3) = 20
    c: Coincident(g2,g3)
    c: DistanceX(g0) = 4
    c: DistanceY(g0) = 77
    c: Coincident(g4,g5)
    c: Coincident(g6,g7)
    c: Coincident(g7,g4)
    c: Horizontal(g6)
    c: DistanceX(g5,g0) = 0
    c: DistanceY(g5,g0) = 7
    c: DistanceX(g2,g4) = 0
    c: DistanceX(g1,g4) = 0
    c: DistanceY(g4,g2) = 7
    c: Horizontal(g4)
    c: Angle(g5) = 1.0472
    c: Horizontal(g8)
    c: Coincident(g9,g8)
    c: Horizontal(g10)
    c: Coincident(g11,g8)
    c: Coincident(g9,g10)
    c: Coincident(g10,g11)
    c: DistanceX(g5,g9) = 0
    c: DistanceX(g10,g6) = 0
    c: DistanceY(g9,g5) = 7
    c: DistanceY(g8,g4) = 7
    c: DistanceX(g8,g4) = 0
    c: DistanceX(g4,g8) = 0
    c: Horizontal(g12)
    c: Coincident(g13,g12)
    c: Horizontal(g14)
    c: Coincident(g15,g12)
    c: Coincident(g1,g2)
    c: Horizontal(g2)
    c: DistanceX(g12,g12) = 2
    c: DistanceX(g9,g12) = 0
    c: DistanceY(g12,g9) = 7
    c: DistanceY(g14,g8) = 7
    c: Coincident(g14,g13)
    c: Coincident(g14,g15)
    c: DistanceX(g14,g8) = 0
    c: DistanceX(g8,g13) = 0
    c: Horizontal(g16)
    c: Coincident(g17,g16)
    c: Horizontal(g18)
    c: Coincident(g19,g16)
    c: DistanceX(g16,g16) = 2
    c: DistanceY(g16,g12) = 7
    c: DistanceX(g12,g16) = 0
    c: DistanceX(g18,g14) = 0
    c: Coincident(g18,g19)
    c: Coincident(g17,g18)
    c: DistanceY(g18,g14) = 7
    c: DistanceX(g18,g18) = 2
    c: Horizontal(g20)
    c: Coincident(g20,g21)
    c: Coincident(g21,g22)
    c: Coincident(g22,g23)
    c: Coincident(g23,g20)
    c: DistanceX(g16,g20) = 0
    c: DistanceY(g20,g16) = 7
    c: DistanceY(g22,g18) = 7
    c: DistanceX(g22,g18) = 0
    c: Horizontal(g22)
    c: DistanceX(g22,g22) = 2
    c: DistanceX(g20,g20) = 2
    c: Horizontal(g24)
    c: Coincident(g25,g24)
    c: Coincident(g26,g25)
    c: Horizontal(g26)
    c: Coincident(g27,g24)
    c: DistanceX(g24,g24) = 2
    c: DistanceX(g0,g24) = 64
    c: DistanceY(g24,g0) = 0
    c: Distance(g25) = 20
    c: Coincident(g26,g27)
    c: Angle(g27) = 2.0944
    c: DistanceX(g26,g26) = 2
    c: Horizontal(g28)
    c: Coincident(g29,g28)
    c: Coincident(g30,g29)
    c: Coincident(g31,g28)
    c: Coincident(g33,g32)
    c: Coincident(g34,g33)
    c: Coincident(g35,g32)
    c: Coincident(g37,g36)
    c: Coincident(g38,g37)
    c: Coincident(g39,g36)
    c: DistanceY(g28,g6) = 0
    c: DistanceY(g32,g9) = 0
    c: DistanceY(g36,g12) = 0
    c: DistanceX(g24,g28) = 0
    c: DistanceX(g32,g28) = 0
    c: DistanceX(g36,g32) = 0
    c: Horizontal(g36)
    c: Horizontal(g32)
    c: DistanceX(g32,g32) = 2
    c: DistanceX(g36,g36) = 2
    c: Horizontal(g30)
    c: Horizontal(g34)
    c: Horizontal(g38)
    c: Coincident(g34,g35)
    c: Coincident(g30,g31)
    c: DistanceX(g25,g30) = 0
    c: DistanceX(g30,g34) = 0
    c: DistanceX(g34,g34) = 2
    c: DistanceX(g30,g30) = 2
    c: Coincident(g38,g39)
    c: DistanceX(g38,g38) = 2
    c: DistanceX(g34,g38) = 0
    c: Horizontal(g40)
    c: Coincident(g41,g40)
    c: Horizontal(g42)
    c: Coincident(g43,g40)
    c: DistanceY(g40,g16) = 0
    c: Horizontal(g44)
    c: Coincident(g45,g44)
    c: Coincident(g46,g45)
    c: Horizontal(g46)
    c: Coincident(g47,g44)
    c: DistanceY(g20,g44) = 0
    c: DistanceX(g44,g40) = 0
    c: DistanceX(g40,g36) = 0
    c: DistanceX(g44,g44) = 2
    c: DistanceX(g40,g40) = 2
    c: DistanceX(g46,g46) = 2
    c: DistanceX(g42,g42) = 2
    c: Coincident(g42,g43)
    c: Coincident(g41,g42)
    c: Coincident(g46,g47)
    c: DistanceX(g42,g38) = 0
    c: DistanceX(g46,g42) = 0
    c: DistanceY(g46,g42) = 7
    c: DistanceY(g42,g38) = 7
    c: DistanceY(g38,g34) = 7
    c: DistanceY(g34,g30) = 7
    c: DistanceY(g30,g25) = 7
    c: DistanceX(g28,g28) = 2
    c: Coincident(g0,g1)
    c: DistanceX(g6,g6) = 2
    c: Coincident(g5,g6)
FEATURE [Part::Extrusion] Extrude007  label="ventsBottomCut"
  Base = -> Sketch007
  Dir = (0,0,1)
  DirMode = 2
  FaceMakerClass = Part::FaceMakerBullseye
  LengthFwd = 20
  LengthRev = 0
  Placement = pos=(0,0,5) rot=(0,0,1;0rad)
  Solid = true
  Symmetric = false
FEATURE [Part::Cylinder] Cylinder016
  Angle = 360
  AttacherType = Attacher::AttachEngine3D
  FirstAngle = 0
  Height = 14
  Placement = pos=(7.25,73.75,2) rot=(0,0,1;0rad)
  Radius = 2.1
  SecondAngle = 0
FEATURE [Part::Cylinder] Cylinder017
  Angle = 360
  AttacherType = Attacher::AttachEngine3D
  FirstAngle = 0
  Height = 14
  Placement = pos=(64.75,38,2) rot=(0,0,1;0rad)
  Radius = 2.1
  SecondAngle = 0
FEATURE [Part::Cylinder] Cylinder018
  Angle = 360
  AttacherType = Attacher::AttachEngine3D
  FirstAngle = 0
  Height = 14
  Placement = pos=(7.25,38,2) rot=(0,0,1;0rad)
  Radius = 2.1
  SecondAngle = 0
FEATURE [Part::Cylinder] Cylinder019
  Angle = 360
  AttacherType = Attacher::AttachEngine3D
  FirstAngle = 0
  Height = 14
  Placement = pos=(64.75,73.75,2) rot=(0,0,1;0rad)
  Radius = 2.1
  SecondAngle = 0
FEATURE [Part::MultiFuse] Fusion009  label="basesM4TopCut"
  Placement = pos=(0,0,12.25) rot=(0,0,1;0rad)
  Shapes = -> [Cylinder019,Cylinder016,Cylinder017,Cylinder018]
FEATURE [Sketcher::SketchObject] Sketch008
  FullyConstrained = true
  MapMode = 2
  Placement = pos=(0,0,12.25) rot=(0,0,1;0rad)
  Support = -> [Fusion009]
  sketch-geometry (10):
    g0: LineSegment StartX=2.5 StartY=78.5 StartZ=0 EndX=2.5 EndY=2.5 EndZ=0
    g1: LineSegment StartX=2.5 StartY=2.5 StartZ=0 EndX=35 EndY=2.5 EndZ=0
    g2: LineSegment StartX=69.5 StartY=21.25 StartZ=0 EndX=69.5 EndY=78.5 EndZ=0
    g3: LineSegment StartX=2.5 StartY=78.5 StartZ=0 EndX=69.5 EndY=78.5 EndZ=0
    g4: LineSegment StartX=35 StartY=2.5 StartZ=0 EndX=35 EndY=3.5 EndZ=0
    g5: LineSegment StartX=35 StartY=3.5 StartZ=0 EndX=3.5 EndY=3.5 EndZ=0
    g6: LineSegment StartX=3.5 StartY=3.5 StartZ=0 EndX=3.5 EndY=77.5 EndZ=0
    g7: LineSegment StartX=3.5 StartY=77.5 StartZ=0 EndX=68.5 EndY=77.5 EndZ=0
    g8: LineSegment StartX=68.5 StartY=77.5 StartZ=0 EndX=68.5 EndY=21.25 EndZ=0
    g9: LineSegment StartX=68.5 StartY=21.25 StartZ=0 EndX=69.5 EndY=21.25 EndZ=0
  constraints (30):
    c: Vertical(g0)
    c: Horizontal(g1)
    c: Vertical(g2)
    c: Coincident(g3,g2)
    c: DistanceX(g-1,g0) = 2.5
    c: DistanceY(g0) = 2.5
    c: Coincident(g1,g0)
    c: Coincident(g0,g3)
    c: Coincident(g4,g1)
    c: Vertical(g4)
    c: Horizontal(g5)
    c: Coincident(g6,g5)
    c: Vertical(g6)
    c: Horizontal(g7)
    c: Coincident(g8,g7)
    c: Vertical(g8)
    c: Coincident(g9,g8)
    c: Coincident(g9,g2)
    c: DistanceX(g5) = 3.5
    c: DistanceY(g-1,g5) = 3.5
    c: DistanceX(g0,g1) = 32.5
    c: Coincident(g5,g4)
    c: Coincident(g6,g7)
    c: DistanceY(g0,g0) = 76
    c: DistanceY(g6,g0) = 1
    c: DistanceX(g7,g2) = 1
    c: DistanceX(g0,g2) = 67
    c: Horizontal(g9)
    c: DistanceY(g8,g7) = 56.25
    c: Horizontal(g3)
FEATURE [Part::Extrusion] Extrude008  label="topAlineIn"
  Base = -> Sketch008
  Dir = (0,0,1)
  DirMode = 2
  FaceMakerClass = Part::FaceMakerBullseye
  LengthFwd = 1.5
  LengthRev = 0
  Placement = pos=(0,0,15) rot=(0,0,1;0rad)
  Solid = true
  Symmetric = false
FEATURE [Part::Cut] Cut002  label="bottom004"
  Base = -> Cut
  Tool = -> Extrude007
FEATURE [Sketcher::SketchObject] Sketch009
  FullyConstrained = true
  MapMode = 4
  Placement = pos=(0,0,0) rot=(0.57735,0.57735,0.57735;2.0944rad)
  sketch-geometry (1):
    g0: Circle CenterX=79 CenterY=2 CenterZ=0 NormalX=0 NormalY=0 NormalZ=1 AngleXU=0 Radius=2
  constraints (3):
    c: DistanceX(g0) = 79
    c: DistanceY(g0) = 2
    c: Radius(g0) = 2
FEATURE [Part::Extrusion] Extrude009  label="bottomInTagHoldIn"
  Base = -> Sketch009
  Dir = (1,0,0)
  DirMode = 2
  FaceMakerClass = Part::FaceMakerBullseye
  LengthFwd = 68
  LengthRev = 0
  Placement = pos=(2,0,0) rot=(0,0,1;0rad)
  Solid = true
  Symmetric = false
FEATURE [Sketcher::SketchObject] Sketch011
  FullyConstrained = true
  Placement = pos=(0,0,0) rot=(0.57735,0.57735,0.57735;2.0944rad)
  sketch-geometry (2):
    g0: Circle CenterX=79 CenterY=2 CenterZ=0 NormalX=0 NormalY=0 NormalZ=1 AngleXU=0 Radius=3
    g1: Circle CenterX=79 CenterY=2 CenterZ=0 NormalX=0 NormalY=0 NormalZ=1 AngleXU=0 Radius=2
  constraints (5):
    c: Radius(g0) = 3
    c: Radius(g1) = 2
    c: Coincident(g0,g1)
    c: DistanceX(g0) = 79
    c: DistanceY(g0) = 2
FEATURE [Part::Extrusion] Extrude011  label="tagBottomCut001"
  Base = -> Sketch011
  Dir = (1,0,0)
  DirMode = 2
  FaceMakerClass = Part::FaceMakerBullseye
  LengthFwd = 10
  LengthRev = 0
  Placement = pos=(31,0,0) rot=(0,0,1;0rad)
  Solid = true
  Symmetric = false
FEATURE [Mesh::Feature] pisugar3_shell_xl
  Placement = pos=(-2.51,33.56,0.54) rot=(-1,0,0;4.71239rad)
FEATURE [Part::MultiFuse] Fusion012  label="bottomIn"
  Shapes = -> [Extrude009,Cut002,Fillet004,Fillet003,Fusion]
FEATURE [Part::MultiFuse] Fusion013  label="bottomCut001"
  Shapes = -> [Extrude011,Extrude004,Fusion007,Fusion001]
FEATURE [Part::Cut] Cut003  label="bottom005"
  Base = -> Fusion012
  Tool = -> Fusion013
FEATURE [Part::MultiFuse] Fusion014  label="topBasesIn"
  Placement = pos=(0,0,18.25) rot=(0,0,1;0rad)
  Shapes = -> [Cylinder008,Cylinder009,Cylinder010,Cylinder011]
FEATURE [Part::MultiFuse] Fusion015  label="topIn"
  Shapes = -> [Fusion014,Extrude008,Fillet005]
FEATURE [Part::MultiFuse] Fusion016  label="topCuts"
  Shapes = -> [Fusion009,Part__Feature060,Box005,Extrude003]
FEATURE [Part::Cut] Cut004  label="top002"
  Base = -> Fusion015
  Tool = -> Fusion016
FEATURE [Part::Fillet] Fillet006  label="hdmi"
  Base = -> Cut003
  Edges = 6 edges r=1: [Edge170,Edge171,Edge172,Edge173,Edge174,Edge175]
FEATURE [Part::Fillet] Fillet007  label="usbInlets"
  Base = -> Fillet006
  Edges = 12 edges r=0.5: [Edge27,Edge28,Edge29,Edge30,Edge31,Edge32,Edge33,Edge34,Edge35,Edge36,Edge37,Edge38]
FEATURE [Part::Fillet] Fillet008  label="bottomInlets"
  Base = -> Fillet007
  Edges = 16 edges r=0.35: [Edge17,Edge18,Edge19,Edge20,Edge21,Edge22,Edge23,Edge24,Edge25,Edge26,Edge27,Edge28,Edge29,Edge30,Edge31,Edge32]
FEATURE [Part::Fillet] Fillet009  label="ventsInsides"
  Base = -> Fillet008
  Edges = 12 edges r=0.15: [Edge266,Edge271,Edge275,Edge279,Edge283,Edge287,Edge305,Edge309,Edge315,Edge317,Edge321,Edge325]
FEATURE [Part::Fillet] Fillet010  label="bottom006"
  Base = -> Fillet009
  Edges = 54 edges: [Edge47 r=1,Edge53 r=0.15,Edge55 r=1,Edge99 r=1,Edge105 r=0.15,Edge107 r=1,Edge109 r=1,Edge115 r=0.15,Edge117 r=1,Edge119 r=1,Edge125 r=0.15,Edge127 r=1,Edge129 r=1,Edge135 r=0.15,Edge137 r=1,Edge139 r=1,Edge145 r=0.15,Edge147 r=1,Edge148 r=1,Edge152 r=1,Edge153 r=1,Edge154 r=1,Edge155 r=1,Edge156 r=1,Edge160 r=1,Edge161 r=1,Edge162 r=0.15,Edge163 r=1,Edge164 r=1,Edge165 r=1,Edge166 r=0.15,Edge167 r=1,Edge168 r=0.15,Edge169 r=1,Edge170 r=1,Edge171 r=1,Edge172 r=1,Edge173 r=1,Edge174 r=0.15,Edge175 r=1,Edge176 r=1,Edge177 r=1,Edge178 r=0.15,Edge179 r=1,Edge180 r=1,Edge181 r=1,Edge182 r=0.15,+7 more]
FEATURE [Sketcher::SketchObject] Sketch012
  FullyConstrained = true
  Placement = pos=(0,0,0) rot=(0.57735,0.57735,0.57735;2.0944rad)
  sketch-geometry (4):
    g0: LineSegment StartX=8 StartY=23 StartZ=0 EndX=26 EndY=23 EndZ=0
    g1: LineSegment StartX=26 StartY=23 StartZ=0 EndX=26 EndY=20 EndZ=0
    g2: LineSegment StartX=26 StartY=20 StartZ=0 EndX=8 EndY=20 EndZ=0
    g3: LineSegment StartX=8 StartY=20 StartZ=0 EndX=8 EndY=23 EndZ=0
  constraints (12):
    c: Coincident(g0,g1)
    c: Coincident(g1,g2)
    c: Coincident(g2,g3)
    c: Coincident(g3,g0)
    c: Horizontal(g0)
    c: Horizontal(g2)
    c: Vertical(g1)
    c: Vertical(g3)
    c: DistanceX(g2) = 8
    c: DistanceX(g2,g0) = 18
    c: DistanceY(g2) = 20
    c: DistanceY(g2,g0) = 3
FEATURE [Part::Extrusion] Extrude012  label="leftInCut"
  Base = -> Sketch012
  Dir = (1,0,0)
  DirMode = 2
  FaceMakerClass = Part::FaceMakerBullseye
  LengthFwd = 2
  LengthRev = 0
  Placement = pos=(70,0,0) rot=(0,0,1;0rad)
  Solid = true
  Symmetric = false
FEATURE [Sketcher::SketchObject] Sketch013
  FullyConstrained = true
  MapMode = 4
  Placement = pos=(70,0,0) rot=(0.57735,0.57735,0.57735;2.0944rad)
  Support = -> [Extrude012]
  sketch-geometry (4):
    g0: LineSegment StartX=26 StartY=19.9 StartZ=0 EndX=12 EndY=19.9 EndZ=0
    g1: LineSegment StartX=12 StartY=19.9 StartZ=0 EndX=12 EndY=22.9 EndZ=0
    g2: LineSegment StartX=12 StartY=22.9 StartZ=0 EndX=26 EndY=22.9 EndZ=0
    g3: LineSegment StartX=26 StartY=22.9 StartZ=0 EndX=26 EndY=19.9 EndZ=0
  constraints (12):
    c: Coincident(g0,g1)
    c: Coincident(g1,g2)
    c: Coincident(g2,g3)
    c: Coincident(g3,g0)
    c: Horizontal(g0)
    c: Horizontal(g2)
    c: Vertical(g1)
    c: Vertical(g3)
    c: DistanceX(g0,g0) = 14
    c: DistanceX(g1) = 12
    c: DistanceY(g1) = 22.9
    c: DistanceY(g1,g1) = 3
FEATURE [Part::Extrusion] Extrude013  label="sdCut"
  Base = -> Sketch013
  Dir = (1,0,0)
  DirMode = 2
  FaceMakerClass = Part::FaceMakerBullseye
  LengthFwd = 2
  LengthRev = 0
  Placement = pos=(-70,0,0) rot=(0,0,1;0rad)
  Solid = true
  Symmetric = false
FEATURE [Part::MultiFuse] Fusion017  label="bottomCutsHor"
  Shapes = -> [Extrude013,Extrude012]
FEATURE [Part::Cut] Cut005  label="bottom007"
  Base = -> Fillet010
  Tool = -> Fusion017
FEATURE [Part::Fillet] Fillet011  label="bottom008"
  Base = -> Cut005
  Edges = 12 edges r=1: [Edge97,Edge98,Edge99,Edge100,Edge275,Edge276,Edge277,Edge278,Edge476,Edge477,Edge478,Edge479]
